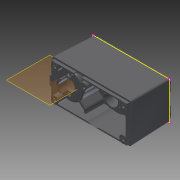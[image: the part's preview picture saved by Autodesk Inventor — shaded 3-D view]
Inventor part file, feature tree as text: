
AUTODESK INVENTOR PART (.ipt)
format: ipt  version: 2013 (Build 170138000, 138)  size: 521,216 bytes
history: native  units: in
note: dims shown in document units (in); Inventor stores cm internally (conversion verified against a paired STEP export)
features: extrude x22, sketch x14, plane x4, fillet x2
ambient origin geometry x8: Origin, YZ Plane, XZ Plane, XY Plane, X Axis, Y Axis, Z Axis, Center Point
bodies: Solid1 (feature_tree)
feature tree (42):
  extrude  "Extrusion1"  Depth=0.051in TaperAngle=0.0deg
  fillet  "Fillet3"  Radius=0.421in
  extrude  "Extrusion2"  Depth=0.051in TaperAngle=0.0deg
  extrude  "Extrusion3"  Depth=0.008in
  sketch  "Sketch5"  dims[d13=0.906in d14=0.0in d15=0.008in]
  extrude  "Extrusion4"  Depth=0.008in
  extrude  "Extrusion5"  Depth=0.1565in TaperAngle=0.0deg
  extrude  "Extrusion6"  Depth=1.0315in TaperAngle=0.0deg
  plane  "Work Plane1"
  extrude  "Extrusion7"  Depth=0.906in TaperAngle=0.0deg
  plane  "Work Plane2"
  plane  "Work Plane3"
  sketch  "Sketch12"  dims[d43=0.311in d44=0.0in d45=0.031in]
  sketch  "Sketch11"  dims[d37=0.1181in d38=0.0in d39=0.1142in d40=0.0in]
  extrude  "Extrusion10"  Depth=0.906in TaperAngle=0.0deg
  fillet  "Fillet2"  Radius=0.1929in
  extrude  "Extrusion11"  Depth=0.1142in TaperAngle=0.0deg
  sketch  "Sketch13"  dims[d46=0.216in d47=0.063in]
  extrude  "Extrusion12"  Depth=0.031in
  extrude  "Extrusion13"  Depth=0.063in
  extrude  "Extrusion14"  Depth=0.197in
  extrude  "Extrusion15"  Depth=0.177in TaperAngle=0.0deg
  extrude  "Extrusion16"  Depth=0.063in
  sketch  "Sketch14"  dims[d48=0.311in d49=0.0in d50=0.197in]
  extrude  "Extrusion17"  Depth=0.0394in
  extrude  "Extrusion18"  Depth=0.177in TaperAngle=0.0deg
  sketch  "Sketch15"  dims[d51=0.177in d52=0.0in d53=0.177in d54=0.0in]
  extrude  "Extrusion20"  Depth=0.177in TaperAngle=0.0deg
  extrude  "Extrusion21"  Depth=0.0395in
  extrude  "Extrusion22"  [1 undecoded]
  extrude  "Extrusion23"  [1 undecoded]
  extrude  "Extrusion24"  [1 undecoded]
  extrude  "Extrusion25"  [1 undecoded]
  sketch  "Sketch16"  dims[d55=0.3298in d56=0.063in d57=0.0394in d58=0.177in d59=0.0in d60=0.177in d61=0.0in d62=0.0395in]
  plane  "Work Plane4"
  sketch  "Sketch1"  dims[d0=0.787in d1=-0.0103in d2=0.051in d3=0.0in d4=0.421in d5=0.0in]
  sketch  "Sketch2"  dims[d6=0.421in d7=0.0in d8=0.051in d9=0.0in]
  sketch  "Sketch4"  dims[d10=0.358in d11=0.0in d12=0.008in]
  sketch  "Sketch6"  dims[d18=-0.1102in d22=0.1565in d23=0.0in]
  sketch  "Sketch8"  dims[d24=0.02in d25=1.0315in d26=0.0in]
  sketch  "Sketch9"  dims[d27=0.906in d28=0.0in d29=0.906in d30=0.0in]
  sketch  "Sketch10"  dims[d31=0.906in d32=0.0in d33=0.906in d34=0.0in d35=0.1929in d36=0.0in]
note: 4 required parameter values undecoded (feature->parameter linkage not recoverable at this tier; creation-order binding heuristic only, values carry confidence <= 0.55)
